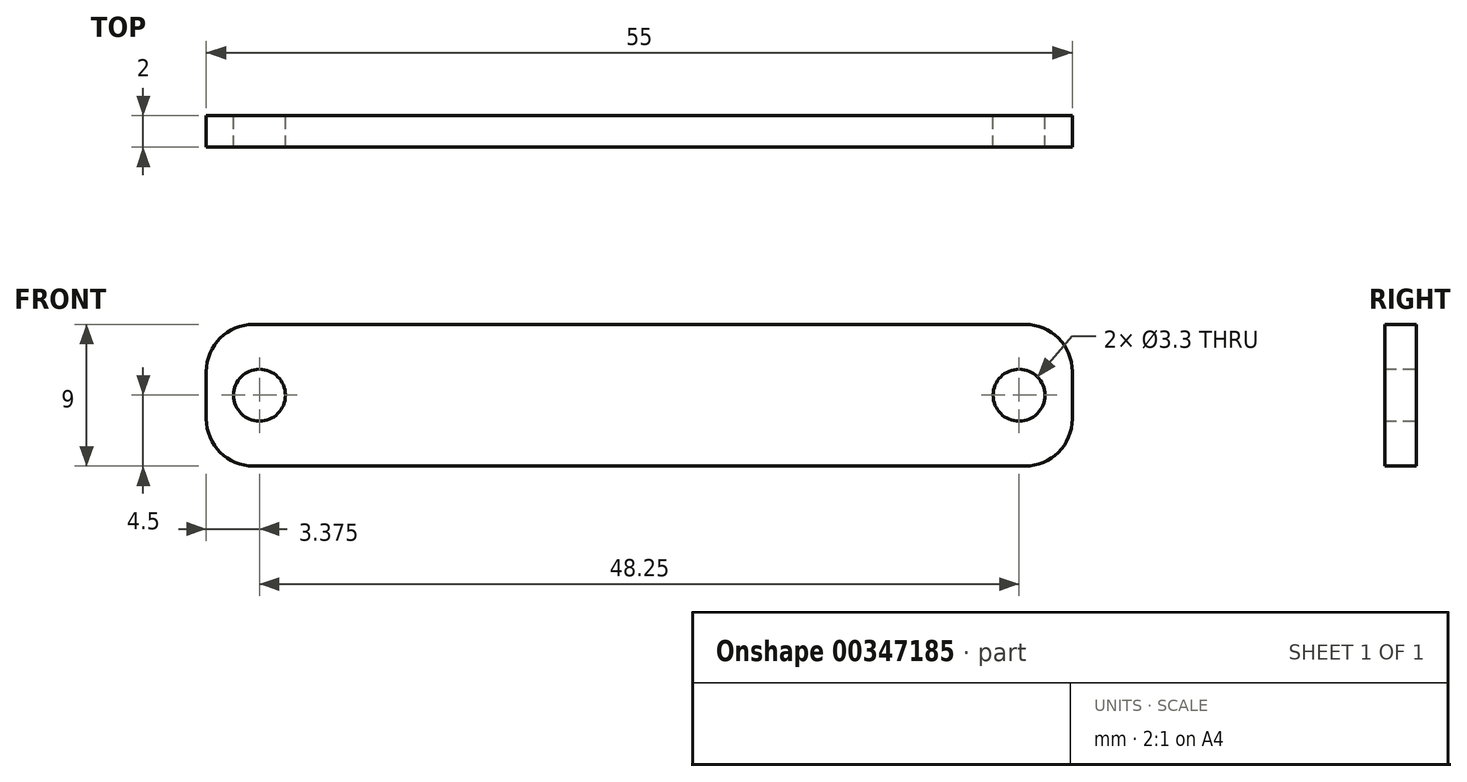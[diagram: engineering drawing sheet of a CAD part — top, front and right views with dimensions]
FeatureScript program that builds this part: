
annotation { "Feature Type Name" : "Feature", "Feature Type Description" : "" }
export const myFeature = defineFeature(function(context is Context, id is Id, definition is map)
    precondition{}
    {
        {
            var Q0;
            Q0=qCreatedBy(makeId("Front.planeOp"),FACE);
            var sketch = newSketch(context, id + "F0", { "sketchPlane" : qUnion([Q0])});
            skLineSegment(sketch, "E0.bottom", {"start": v(24.5, -4.5) * mm, "end": v(-24.5, -4.5) * mm});
            skLineSegment(sketch, "E0.top", {"start": v(24.5, 4.5) * mm, "end": v(-24.5, 4.5) * mm});
            skLineSegment(sketch, "E0.left", {"start": v(27.5, -1.5) * mm, "end": v(27.5, 1.5) * mm});
            skLineSegment(sketch, "E0.right", {"start": v(-27.5, -1.5) * mm, "end": v(-27.5, 1.5) * mm});
            skPoint(sketch, "E0.middle", {"position": v(0, 0) * mm});
            skPoint(sketch, "E1", {"position": v(-24.12, 0) * mm});
            skPoint(sketch, "E2", {"position": v(24.12, 0) * mm});
            skPoint(sketch, "E3.visualSharp", {"position": v(27.5, 4.5) * mm});
            skArc(sketch, "E3.filletArc", {"start": v(27.5, 1.5) * mm, "mid": v(26.62, 3.62) * mm, "end": v(24.5, 4.5) * mm});
            skPoint(sketch, "E4.visualSharp", {"position": v(27.5, -4.5) * mm});
            skArc(sketch, "E4.filletArc", {"start": v(24.5, -4.5) * mm, "mid": v(26.62, -3.62) * mm, "end": v(27.5, -1.5) * mm});
            skPoint(sketch, "E5.visualSharp", {"position": v(-27.5, 4.5) * mm});
            skArc(sketch, "E5.filletArc", {"start": v(-24.5, 4.5) * mm, "mid": v(-26.62, 3.62) * mm, "end": v(-27.5, 1.5) * mm});
            skPoint(sketch, "E6.visualSharp", {"position": v(-27.5, -4.5) * mm});
            skArc(sketch, "E6.filletArc", {"start": v(-27.5, -1.5) * mm, "mid": v(-26.62, -3.62) * mm, "end": v(-24.5, -4.5) * mm});
            skSolve(sketch);
        }
        {
            var Q0;
            Q0=makeQuery(id+"F0.imprint","IMPRINT",FACE,{"disambiguationData":[TD([[makeQuery(id+"F0.imprint","IMPRINT",EDGE,{"derivedFrom":sQuery(id+"F0.wireOp",EDGE,"E0.bottom")}),-1.0]])]});
            extrude(context, id + "F1", {"entities" : qUnion([Q0]), "depth" : 2 * mm});
        }
        {
            var Q0;
            Q0=sQuery(id+"F0.wireOp",VERTEX,"E2");
            var Q1;
            Q1=sQuery(id+"F0.wireOp",VERTEX,"E1");
            var Q2;
            Q2=makeQuery(id+"F1.opExtrude","SWEPT_BODY",BODY,{"disambiguationData":[OSD([sQuery(id+"F0.wireOp",EDGE,"E0.bottom"),sQuery(id+"F0.wireOp",EDGE,"E0.top"),sQuery(id+"F0.wireOp",EDGE,"E0.left"),sQuery(id+"F0.wireOp",EDGE,"E0.right"),sQuery(id+"F0.wireOp",EDGE,"E3.filletArc"),sQuery(id+"F0.wireOp",EDGE,"E4.filletArc"),sQuery(id+"F0.wireOp",EDGE,"E5.filletArc"),sQuery(id+"F0.wireOp",EDGE,"E6.filletArc")])]});
            hole(context, id + "F2", {"style" : HoleStyle.SIMPLE, "endStyle" : HoleEndStyle.BLIND, "oppositeDirection" : true, "standardTappedOrClearance" : lookupTablePath({ "standard" : "ISO", "fit" : "Normal", "size" : "M3", "type" : "Clearance" }), "standardBlindInLast" : lookupTablePath({ "fit" : "Standard", "standard" : "ISO", "size" : "M3", "type" : "Clearance" }), "holeDiameter" : 3.3 * mm, "holeDepth" : 13.5 * mm, "tappedDepth" : 12 * mm, "tapClearance" : 3, "locations" : qUnion([Q0, Q1]), "scope" : qUnion([Q2])});
        }
    });
